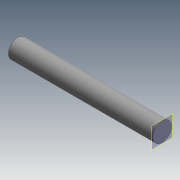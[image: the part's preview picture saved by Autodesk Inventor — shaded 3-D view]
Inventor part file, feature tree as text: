
AUTODESK INVENTOR PART (.ipt)
format: ipt  version: 2014 SP1 (Build 180222100, 222)  size: 68,608 bytes
history: native  units: in
note: dims shown in document units (in); Inventor stores cm internally (conversion verified against a paired STEP export)
features: plane x1, extrude x1, thread x1, sketch x1
ambient origin geometry x8: Origin, YZ Plane, XZ Plane, XY Plane, X Axis, Y Axis, Z Axis, Center Point
bodies: Solid1 (feature_tree)
feature tree (4):
  plane  "Work Plane1"
  extrude  "Extrusion1"  Depth=0.3937in TaperAngle=0.0deg
  thread  "Thread1"  [1 undecoded]
  sketch  "Sketch1"  dims[d0=4.061in d1=0.0in d2=0.3937in d3=0.0in]
note: 1 required parameter value undecoded (feature->parameter linkage not recoverable at this tier; creation-order binding heuristic only, values carry confidence <= 0.55)
